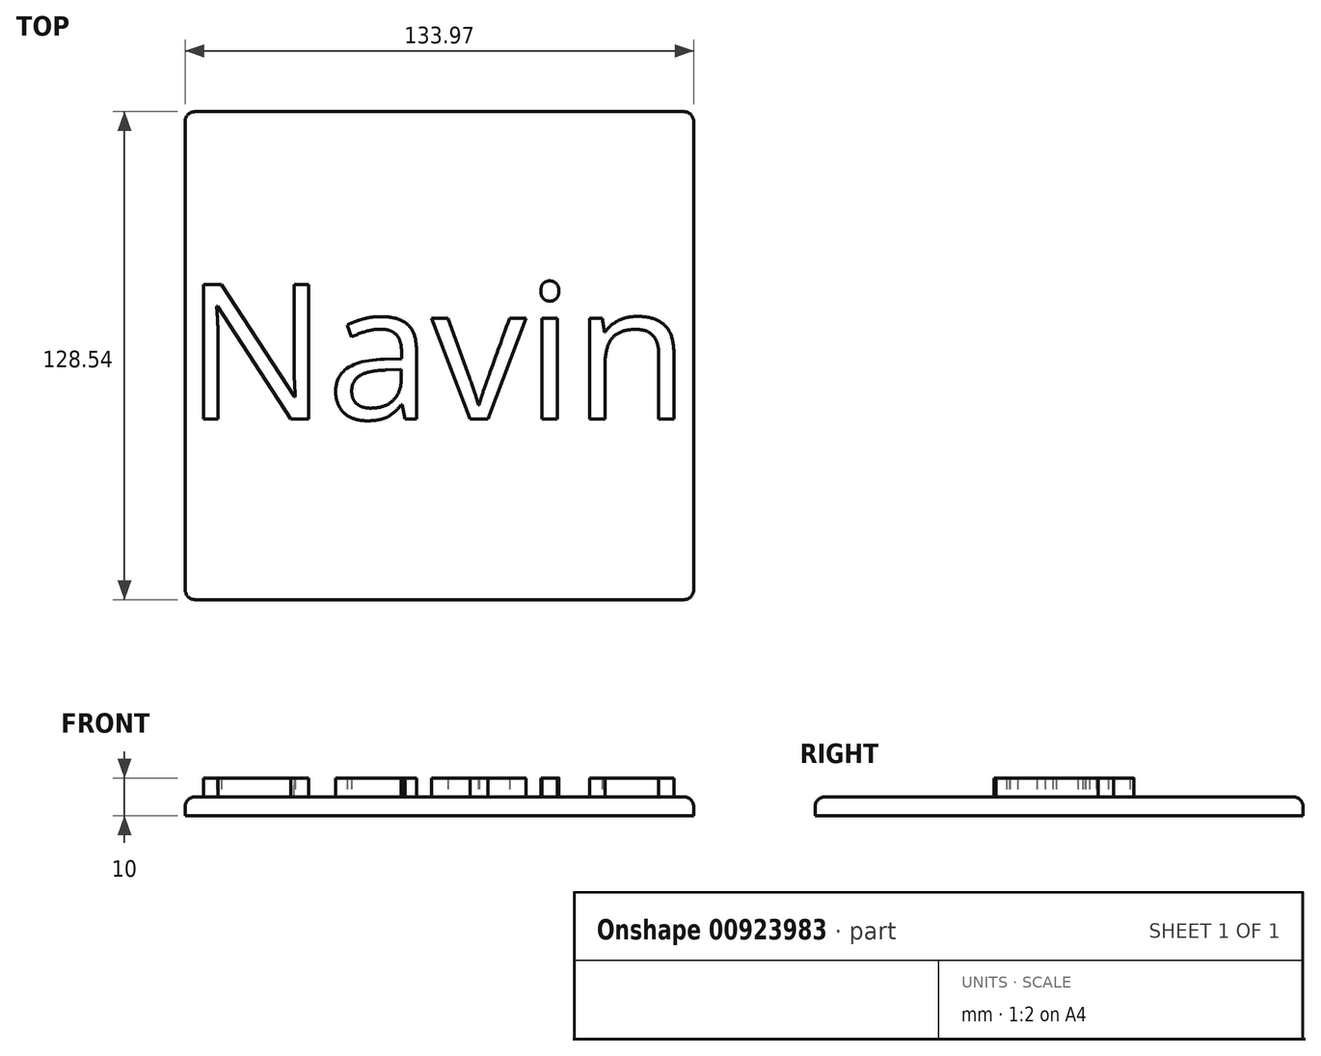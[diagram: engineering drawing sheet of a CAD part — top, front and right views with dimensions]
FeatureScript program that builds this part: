
annotation { "Feature Type Name" : "Feature", "Feature Type Description" : "" }
export const myFeature = defineFeature(function(context is Context, id is Id, definition is map)
    precondition{}
    {
        {
            var Q0;
            Q0=qCreatedBy(makeId("Top.planeOp"),FACE);
            var sketch = newSketch(context, id + "F0", { "sketchPlane" : qUnion([Q0])});
            skLineSegment(sketch, "E0.bottom", {"start": v(-69.97, 68.57) * mm, "end": v(64, 68.57) * mm});
            skLineSegment(sketch, "E0.top", {"start": v(-69.97, -59.97) * mm, "end": v(64, -59.97) * mm});
            skLineSegment(sketch, "E0.left", {"start": v(-69.97, 68.57) * mm, "end": v(-69.97, -59.97) * mm});
            skLineSegment(sketch, "E0.right", {"start": v(64, 68.57) * mm, "end": v(64, -59.97) * mm});
            skSolve(sketch);
        }
        {
            var Q0;
            Q0=makeQuery(id+"F0.imprint","IMPRINT",FACE,{"disambiguationData":[TD([[makeQuery(id+"F0.imprint","IMPRINT",EDGE,{"derivedFrom":sQuery(id+"F0.wireOp",EDGE,"E0.bottom")}),-1.0]])]});
            extrude(context, id + "F1", {"entities" : qUnion([Q0]), "depth" : 5 * mm, "offsetDistance" : 25.4 * mm});
        }
        {
            var Q0;
            Q0=makeQuery(id+"F1.opExtrude","CAP_FACE",FACE,{"disambiguationData":[OSD([sQuery(id+"F0.wireOp",EDGE,"E0.bottom"),sQuery(id+"F0.wireOp",EDGE,"E0.top"),sQuery(id+"F0.wireOp",EDGE,"E0.left"),sQuery(id+"F0.wireOp",EDGE,"E0.right")])],"isStart":false});
            var sketch = newSketch(context, id + "F2", { "sketchPlane" : qUnion([Q0])});
            skText(sketch, "E1", { "text": "Navin", "fontName": "OpenSans-Regular.ttf"});
            const initialGuessF2  = {"E1": [-0.06997, -0.01238, 1, 0, 0.03569]};
            skSetInitialGuess(sketch, initialGuessF2);
            skSolve(sketch);
        }
        {
            var Q0;
            Q0 = qSketchRegion(id + "F2", true);
            extrude(context, id + "F3", {"entities" : qUnion([Q0]), "operationType" : NewBodyOperationType.ADD, "depth" : 5 * mm, "offsetDistance" : 25.4 * mm});
        }
        {
            var Q0;
            Q0=makeQuery(id+"F1.opExtrude","CAP_EDGE",EDGE,{"disambiguationData":[OSD([sQuery(id+"F0.wireOp",EDGE,"E0.top")])],"isStart":false});
            fillet(context, id + "F4", {"entities" : qUnion([Q0]), "radius" : 2.54 * mm, "tangentPropagation" : true, "allowEdgeOverflow" : false});
        }
        {
            var Q0;
            Q0=makeQuery(id+"F1.opExtrude","CAP_EDGE",EDGE,{"disambiguationData":[OSD([sQuery(id+"F0.wireOp",EDGE,"E0.right")])],"isStart":false});
            fillet(context, id + "F5", {"entities" : qUnion([Q0]), "radius" : 2.54 * mm, "tangentPropagation" : true, "allowEdgeOverflow" : false});
        }
        {
            var Q0;
            Q0=makeQuery(id+"F1.opExtrude","CAP_EDGE",EDGE,{"disambiguationData":[OSD([sQuery(id+"F0.wireOp",EDGE,"E0.left")])],"isStart":false});
            fillet(context, id + "F6", {"entities" : qUnion([Q0]), "radius" : 2.54 * mm, "tangentPropagation" : true, "allowEdgeOverflow" : false});
        }
        {
            var Q0;
            Q0=makeQuery(id+"F1.opExtrude","CAP_EDGE",EDGE,{"disambiguationData":[OSD([sQuery(id+"F0.wireOp",EDGE,"E0.bottom")])],"isStart":false});
            fillet(context, id + "F7", {"entities" : qUnion([Q0]), "radius" : 2.54 * mm, "tangentPropagation" : true, "allowEdgeOverflow" : false});
        }
    });
